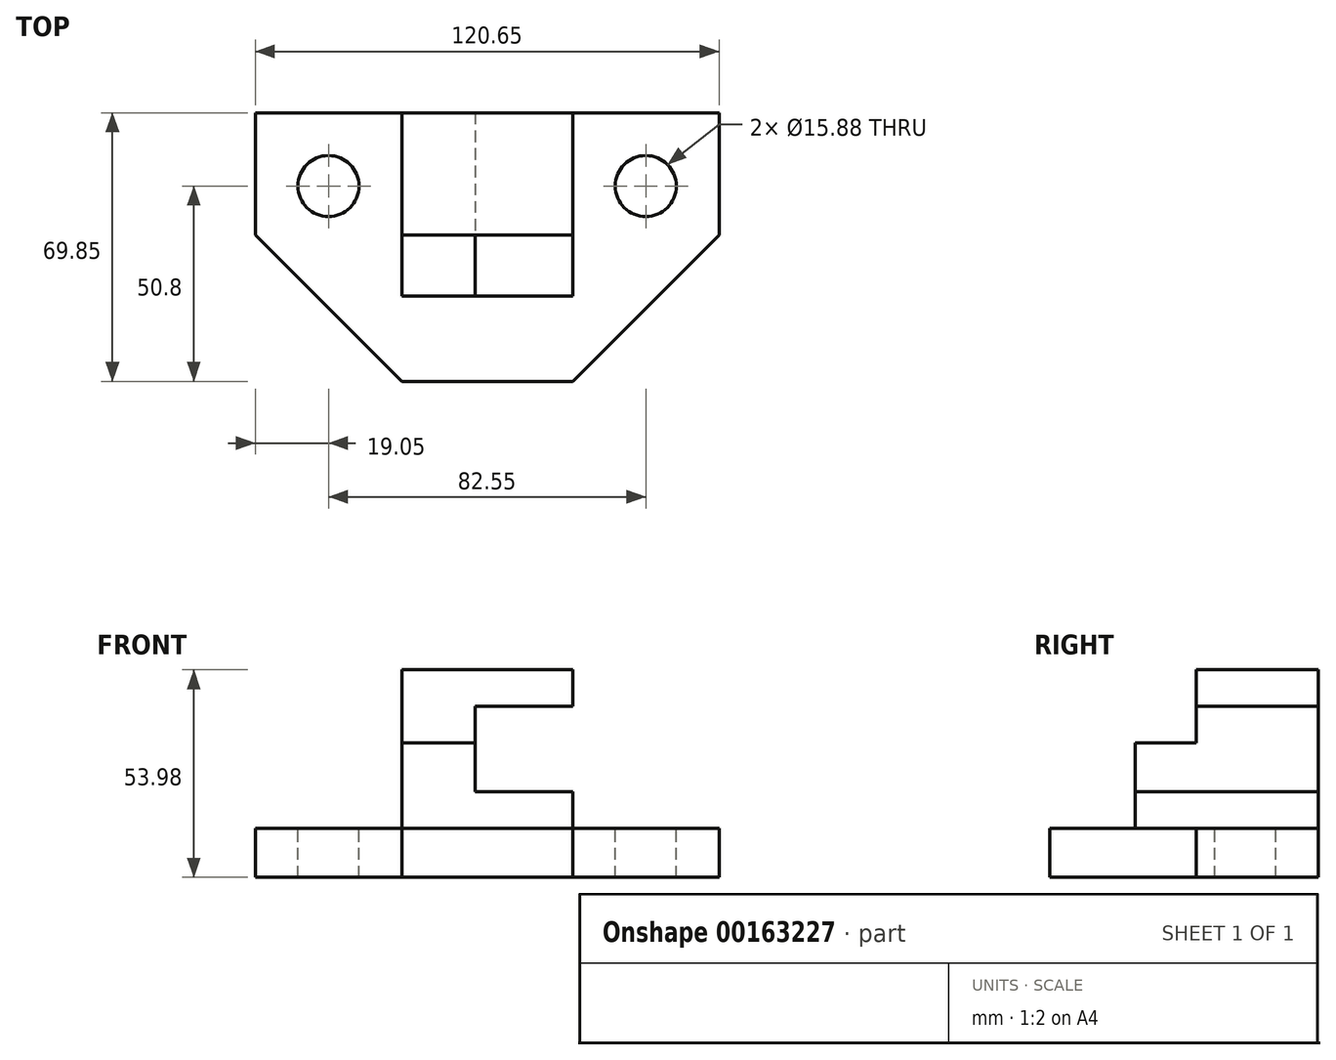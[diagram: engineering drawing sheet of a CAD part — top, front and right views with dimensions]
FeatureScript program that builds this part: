
annotation { "Feature Type Name" : "Feature", "Feature Type Description" : "" }
export const myFeature = defineFeature(function(context is Context, id is Id, definition is map)
    precondition{}
    {
        {
            var Q0;
            Q0=qCreatedBy(makeId("Top.planeOp"),FACE);
            var sketch = newSketch(context, id + "F0", { "sketchPlane" : qUnion([Q0])});
            skLineSegment(sketch, "E0", {"start": v(0, 0) * mm, "end": v(120.65, 0) * mm});
            skLineSegment(sketch, "E1", {"start": v(120.65, 0) * mm, "end": v(120.65, -31.75) * mm});
            skLineSegment(sketch, "E2", {"start": v(120.65, -31.75) * mm, "end": v(82.55, -69.85) * mm});
            skLineSegment(sketch, "E3", {"start": v(82.55, -69.85) * mm, "end": v(38.1, -69.85) * mm});
            skLineSegment(sketch, "E4", {"start": v(38.1, -69.85) * mm, "end": v(0, -31.75) * mm});
            skLineSegment(sketch, "E5", {"start": v(0, -31.75) * mm, "end": v(0, 0) * mm});
            skSolve(sketch);
        }
        {
            var Q0;
            Q0=makeQuery(id+"F0.imprint","IMPRINT",FACE,{"disambiguationData":[TD([[makeQuery(id+"F0.imprint","IMPRINT",EDGE,{"derivedFrom":sQuery(id+"F0.wireOp",EDGE,"E0")}),-1.0]])]});
            extrude(context, id + "F1", {"entities" : qUnion([Q0]), "depth" : 12.7 * mm});
        }
        {
            var Q0;
            Q0=makeQuery(id+"F1.opExtrude","CAP_FACE",FACE,{"disambiguationData":[OSD([sQuery(id+"F0.wireOp",EDGE,"E0"),sQuery(id+"F0.wireOp",EDGE,"E1"),sQuery(id+"F0.wireOp",EDGE,"E2"),sQuery(id+"F0.wireOp",EDGE,"E3"),sQuery(id+"F0.wireOp",EDGE,"E4"),sQuery(id+"F0.wireOp",EDGE,"E5")])],"isStart":false});
            var sketch = newSketch(context, id + "F2", { "sketchPlane" : qUnion([Q0])});
            skPoint(sketch, "E6", {"position": v(19.05, -19.05) * mm});
            skPoint(sketch, "E7", {"position": v(101.6, -19.05) * mm});
            skSolve(sketch);
        }
        {
            var Q0;
            Q0=sQuery(id+"F2.wireOp",VERTEX,"E6");
            var Q1;
            Q1=sQuery(id+"F2.wireOp",VERTEX,"E7");
            var Q2;
            Q2=makeQuery(id+"F1.opExtrude","SWEPT_BODY",BODY,{"disambiguationData":[OSD([sQuery(id+"F0.wireOp",EDGE,"E0"),sQuery(id+"F0.wireOp",EDGE,"E1"),sQuery(id+"F0.wireOp",EDGE,"E2"),sQuery(id+"F0.wireOp",EDGE,"E3"),sQuery(id+"F0.wireOp",EDGE,"E4"),sQuery(id+"F0.wireOp",EDGE,"E5")])]});
            hole(context, id + "F3", {"style" : HoleStyle.SIMPLE, "endStyle" : HoleEndStyle.THROUGH, "holeDiameter" : 15.88 * mm, "locations" : qUnion([Q0, Q1]), "scope" : qUnion([Q2]), "isTappedThrough" : true});
        }
        {
            var Q0;
            Q0=makeQuery(id+"F1.opExtrude","CAP_FACE",FACE,{"disambiguationData":[OSD([sQuery(id+"F0.wireOp",EDGE,"E0"),sQuery(id+"F0.wireOp",EDGE,"E1"),sQuery(id+"F0.wireOp",EDGE,"E2"),sQuery(id+"F0.wireOp",EDGE,"E3"),sQuery(id+"F0.wireOp",EDGE,"E4"),sQuery(id+"F0.wireOp",EDGE,"E5")])],"isStart":false});
            var sketch = newSketch(context, id + "F4", { "sketchPlane" : qUnion([Q0])});
            skLineSegment(sketch, "E8.bottom", {"start": v(82.55, 0) * mm, "end": v(38.1, 0) * mm});
            skLineSegment(sketch, "E8.top", {"start": v(82.55, -31.75) * mm, "end": v(38.1, -31.75) * mm});
            skLineSegment(sketch, "E8.left", {"start": v(82.55, 0) * mm, "end": v(82.55, -31.75) * mm});
            skLineSegment(sketch, "E8.right", {"start": v(38.1, 0) * mm, "end": v(38.1, -31.75) * mm});
            skSolve(sketch);
        }
        {
            var Q0;
            Q0=makeQuery(id+"F4.imprint","IMPRINT",FACE,{"disambiguationData":[TD([[makeQuery(id+"F4.imprint","IMPRINT",EDGE,{"derivedFrom":sQuery(id+"F4.wireOp",EDGE,"E8.bottom")}),-1.0]])]});
            extrude(context, id + "F5", {"entities" : qUnion([Q0]), "operationType" : NewBodyOperationType.ADD, "depth" : 41.27 * mm});
        }
        {
            var Q0;
            Q0=makeQuery(id+"F5.opExtrude","SWEPT_FACE",FACE,{"disambiguationData":[OSD([sQuery(id+"F4.wireOp",EDGE,"E8.top")])]});
            var sketch = newSketch(context, id + "F6", { "sketchPlane" : qUnion([Q0])});
            skLineSegment(sketch, "E9.bottom", {"start": v(82.55, 44.45) * mm, "end": v(57.15, 44.45) * mm});
            skLineSegment(sketch, "E9.top", {"start": v(82.55, 22.23) * mm, "end": v(57.15, 22.23) * mm});
            skLineSegment(sketch, "E9.left", {"start": v(82.55, 44.45) * mm, "end": v(82.55, 22.23) * mm});
            skLineSegment(sketch, "E9.right", {"start": v(57.15, 44.45) * mm, "end": v(57.15, 22.23) * mm});
            skSolve(sketch);
        }
        {
            var Q0;
            Q0=makeQuery(id+"F5.opExtrude","CAP_FACE",FACE,{"disambiguationData":[OSD([sQuery(id+"F4.wireOp",EDGE,"E8.bottom"),sQuery(id+"F4.wireOp",EDGE,"E8.top"),sQuery(id+"F4.wireOp",EDGE,"E8.left"),sQuery(id+"F4.wireOp",EDGE,"E8.right")])],"isStart":false});
            var sketch = newSketch(context, id + "F7", { "sketchPlane" : qUnion([Q0])});
            skLineSegment(sketch, "E10.bottom", {"start": v(38.1, -31.75) * mm, "end": v(82.55, -31.75) * mm});
            skLineSegment(sketch, "E10.top", {"start": v(38.1, -47.62) * mm, "end": v(82.55, -47.62) * mm});
            skLineSegment(sketch, "E10.left", {"start": v(38.1, -31.75) * mm, "end": v(38.1, -47.62) * mm});
            skLineSegment(sketch, "E10.right", {"start": v(82.55, -31.75) * mm, "end": v(82.55, -47.62) * mm});
            skSolve(sketch);
        }
        {
            var Q0;
            Q0=makeQuery(id+"F7.imprint","IMPRINT",FACE,{"disambiguationData":[TD([[makeQuery(id+"F7.imprint","IMPRINT",EDGE,{"derivedFrom":sQuery(id+"F7.wireOp",EDGE,"E10.bottom")}),1.0]])]});
            var Q1;
            Q1=makeQuery(id+"F1.opExtrude","CAP_FACE",FACE,{"disambiguationData":[OSD([sQuery(id+"F0.wireOp",EDGE,"E0"),sQuery(id+"F0.wireOp",EDGE,"E1"),sQuery(id+"F0.wireOp",EDGE,"E2"),sQuery(id+"F0.wireOp",EDGE,"E3"),sQuery(id+"F0.wireOp",EDGE,"E4"),sQuery(id+"F0.wireOp",EDGE,"E5")])],"isStart":false});
            extrude(context, id + "F8", {"entities" : qUnion([Q0]), "operationType" : NewBodyOperationType.ADD, "endBound" : BoundingType.UP_TO_SURFACE, "oppositeDirection" : true, "endBoundEntityFace" : qUnion([Q1]), "depth" : 25.4 * mm, "hasSecondDirection" : true, "secondDirectionOppositeDirection" : true, "secondDirectionDepth" : 19.05 * mm});
        }
        {
            var Q0;
            Q0=makeQuery(id+"F6.imprint","IMPRINT",FACE,{"disambiguationData":[TD([[makeQuery(id+"F6.imprint","IMPRINT",EDGE,{"derivedFrom":sQuery(id+"F6.wireOp",EDGE,"E9.bottom")}),1.0]])]});
            extrude(context, id + "F9", {"entities" : qUnion([Q0]), "operationType" : NewBodyOperationType.REMOVE, "endBound" : BoundingType.THROUGH_ALL, "oppositeDirection" : true, "depth" : 25.4 * mm, "hasSecondDirection" : true, "secondDirectionBound" : SecondDirectionBoundingType.THROUGH_ALL, "secondDirectionOppositeDirection" : false, "secondDirectionDepth" : 27.18 * mm});
        }
    });
